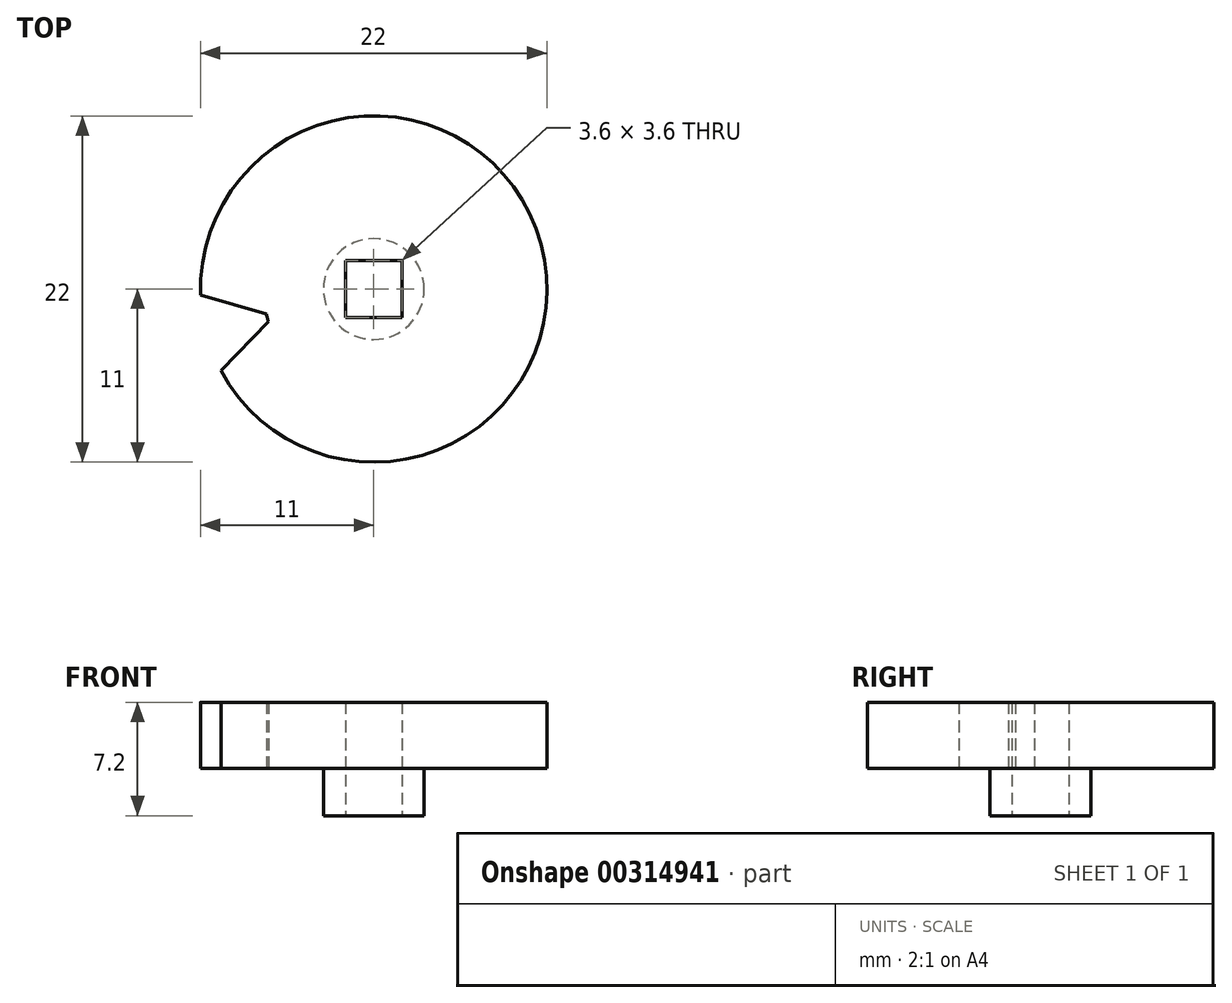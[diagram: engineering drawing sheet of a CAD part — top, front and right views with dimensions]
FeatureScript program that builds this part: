
annotation { "Feature Type Name" : "Feature", "Feature Type Description" : "" }
export const myFeature = defineFeature(function(context is Context, id is Id, definition is map)
    precondition{}
    {
        {
            var Q0;
            Q0=qCreatedBy(makeId("Top.planeOp"),FACE);
            var sketch = newSketch(context, id + "F0", { "sketchPlane" : qUnion([Q0])});
            skCircle(sketch, "E0", {"center": v(0, 0) * mm, "radius": 11 * mm});
            skSolve(sketch);
        }
        {
            var Q0;
            Q0 = qSketchRegion(id + "F0", true);
            extrude(context, id + "F1", {"entities" : qUnion([Q0]), "depth" : 4.2 * mm});
        }
        {
            var Q0;
            Q0=makeQuery(id+"F1.opExtrude","CAP_FACE",FACE,{"disambiguationData":[OSD([sQuery(id+"F0.wireOp",EDGE,"E0")])],"isStart":true});
            var sketch = newSketch(context, id + "F2", { "sketchPlane" : qUnion([Q0])});
            skLineSegment(sketch, "E1", {"start": v(0, 0) * mm, "end": v(-10.62, 2.86) * mm});
            skLineSegment(sketch, "E2", {"start": v(0, 0) * mm, "end": v(-6.82, 1.58) * mm});
            skLineSegment(sketch, "E3", {"start": v(0, 0) * mm, "end": v(-6.7, 2.05) * mm});
            skLineSegment(sketch, "E4", {"start": v(0, 0) * mm, "end": v(-9.7, 5.18) * mm});
            skLineSegment(sketch, "E5", {"start": v(0, 0) * mm, "end": v(-11, 0.4) * mm});
            skArc(sketch, "E6", {"start": v(-6.7, 2.05) * mm, "mid": v(-6.76, 1.82) * mm, "end": v(-6.82, 1.58) * mm});
            skArc(sketch, "E7", {"start": v(-9.7, 5.18) * mm, "mid": v(-10.62, 2.86) * mm, "end": v(-11, 0.4) * mm});
            skLineSegment(sketch, "E8", {"start": v(-11, 0.4) * mm, "end": v(-6.82, 1.58) * mm});
            skLineSegment(sketch, "E9", {"start": v(-9.7, 5.18) * mm, "end": v(-6.7, 2.05) * mm});
            skSolve(sketch);
        }
        {
            var Q0;
            {var subQ5=sQuery(id+"F2.wireOp",EDGE,"E8");Q0=makeQuery(id+"F2.imprint","IMPRINT",FACE,{"disambiguationData":[TD([[makeQuery(id+"F2.imprint","IMPRINT",EDGE,{"derivedFrom":subQ5}),1.0]])]});}
            var Q1;
            {var subQ5=sQuery(id+"F2.wireOp",EDGE,"E9");Q1=makeQuery(id+"F2.imprint","IMPRINT",FACE,{"disambiguationData":[TD([[makeQuery(id+"F2.imprint","IMPRINT",EDGE,{"derivedFrom":subQ5}),-1.0]])]});}
            extrude(context, id + "F3", {"entities" : qUnion([Q0, Q1]), "operationType" : NewBodyOperationType.REMOVE, "oppositeDirection" : true, "depth" : 25 * mm});
        }
        {
            var Q0;
            Q0=qCreatedBy(makeId("Right.planeOp"),FACE);
            var sketch = newSketch(context, id + "F4", { "sketchPlane" : qUnion([Q0])});
            skLineSegment(sketch, "E10", {"start": v(0, 0) * mm, "end": v(0, -17.89) * mm});
            skSolve(sketch);
        }
        {
            var Q0;
            Q0=makeQuery(id+"F1.opExtrude","CAP_FACE",FACE,{"disambiguationData":[OSD([sQuery(id+"F0.wireOp",EDGE,"E0")])],"isStart":true});
            var sketch = newSketch(context, id + "F5", { "sketchPlane" : qUnion([Q0])});
            skCircle(sketch, "E11", {"center": v(0, 0) * mm, "radius": 3.2 * mm});
            skSolve(sketch);
        }
        {
            var Q0;
            Q0 = qSketchRegion(id + "F5", true);
            extrude(context, id + "F6", {"entities" : qUnion([Q0]), "operationType" : NewBodyOperationType.ADD, "depth" : 3 * mm});
        }
        {
            var Q0;
            Q0=makeQuery(id+"F6.opExtrude","CAP_FACE",FACE,{"disambiguationData":[OSD([sQuery(id+"F5.wireOp",EDGE,"E11")])],"isStart":false});
            var sketch = newSketch(context, id + "F7", { "sketchPlane" : qUnion([Q0])});
            skLineSegment(sketch, "E12.bottom", {"start": v(1.8, 1.8) * mm, "end": v(-1.8, 1.8) * mm});
            skLineSegment(sketch, "E12.top", {"start": v(1.8, -1.8) * mm, "end": v(-1.8, -1.8) * mm});
            skLineSegment(sketch, "E12.left", {"start": v(1.8, 1.8) * mm, "end": v(1.8, -1.8) * mm});
            skLineSegment(sketch, "E12.right", {"start": v(-1.8, 1.8) * mm, "end": v(-1.8, -1.8) * mm});
            skPoint(sketch, "E12.middle", {"position": v(0, 0) * mm});
            skSolve(sketch);
        }
        {
            var Q0;
            Q0 = qSketchRegion(id + "F7", true);
            extrude(context, id + "F8", {"entities" : qUnion([Q0]), "operationType" : NewBodyOperationType.REMOVE, "endBound" : BoundingType.THROUGH_ALL, "oppositeDirection" : true, "depth" : 25 * mm});
        }
    });
